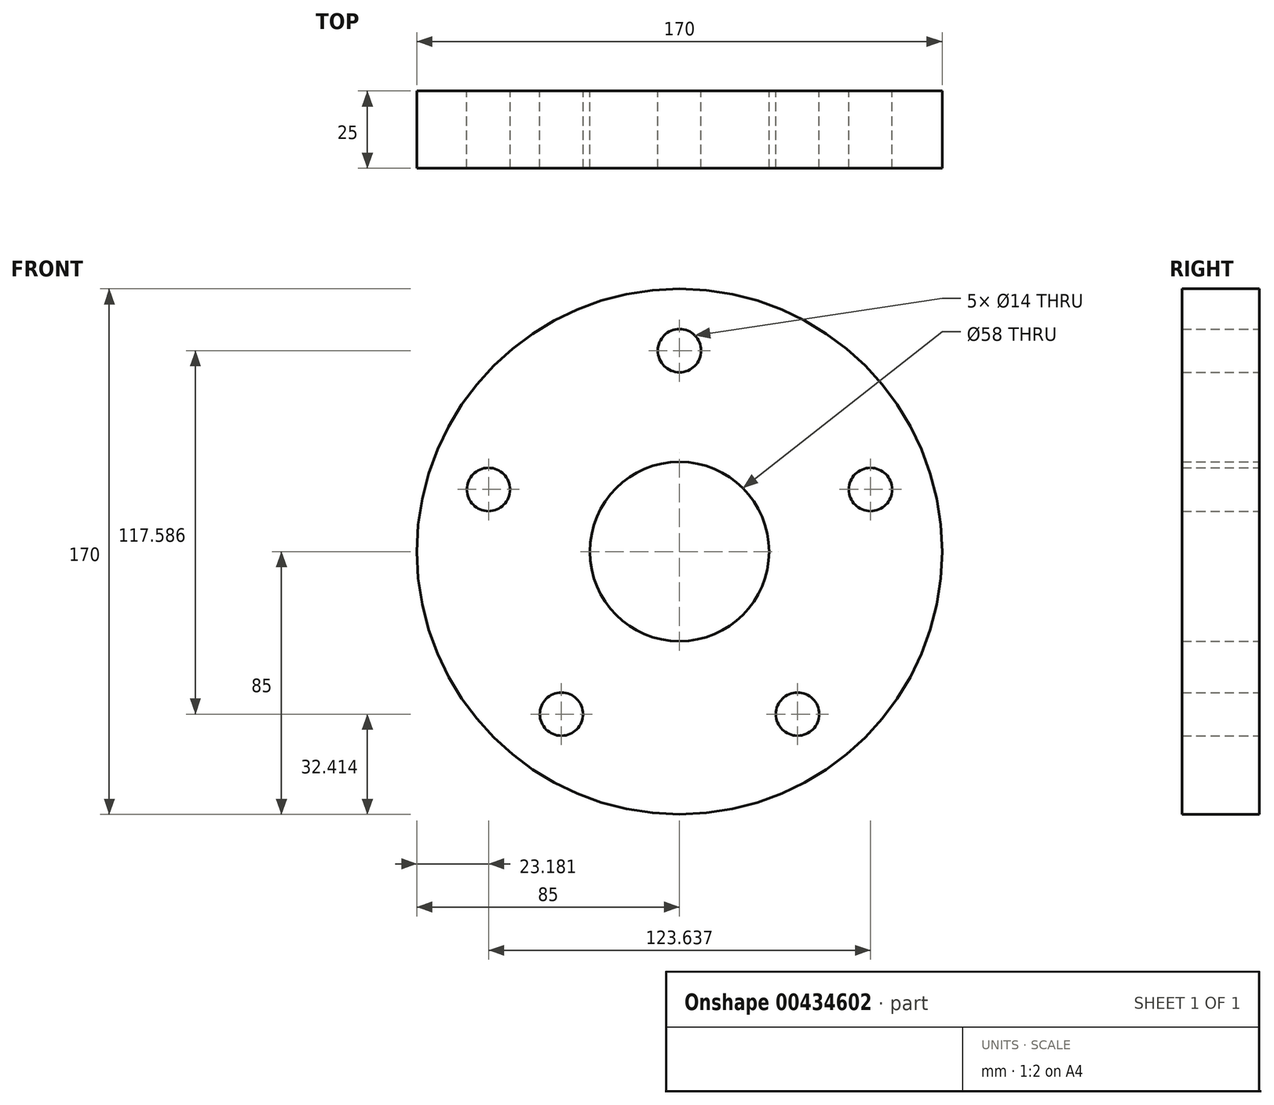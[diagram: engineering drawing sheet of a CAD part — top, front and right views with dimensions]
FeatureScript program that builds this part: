
annotation { "Feature Type Name" : "Feature", "Feature Type Description" : "" }
export const myFeature = defineFeature(function(context is Context, id is Id, definition is map)
    precondition{}
    {
        {
            var Q0;
            Q0=qCreatedBy(makeId("Front.planeOp"),FACE);
            var sketch = newSketch(context, id + "F0", { "sketchPlane" : qUnion([Q0])});
            skCircle(sketch, "E0", {"center": v(0, 0) * mm, "radius": 29 * mm});
            skCircle(sketch, "E1", {"center": v(0, 0) * mm, "radius": 85 * mm});
            skLineSegment(sketch, "E2", {"start": v(0, -97.05) * mm, "end": v(0, 101.44) * mm, "construction": true});
            skCircle(sketch, "E3", {"center": v(0, 65) * mm, "radius": 7 * mm});
            skCircle(sketch, "E4", {"center": v(0, 0) * mm, "radius": 65 * mm, "construction": true});
            skCircle(sketch, "E5.1.0", {"center": v(-61.82, 20.09) * mm, "radius": 7 * mm});
            skCircle(sketch, "E5.2.0", {"center": v(-38.2, -52.59) * mm, "radius": 7 * mm});
            skCircle(sketch, "E5.3.0", {"center": v(38.2, -52.59) * mm, "radius": 7 * mm});
            skCircle(sketch, "E5.4.0", {"center": v(61.82, 20.09) * mm, "radius": 7 * mm});
            skSolve(sketch);
        }
        {
            var Q0;
            Q0 = qSketchRegion(id + "F0", true);
            extrude(context, id + "F1", {"entities" : qUnion([Q0]), "depth" : 25 * mm});
        }
        {
            var Q0;
            Q0=makeQuery(id+"F1.opExtrude","CAP_FACE",FACE,{"disambiguationData":[OSD([sQuery(id+"F0.wireOp",EDGE,"E0"),sQuery(id+"F0.wireOp",EDGE,"E1"),sQuery(id+"F0.wireOp",EDGE,"E3"),sQuery(id+"F0.wireOp",EDGE,"E5.1.0"),sQuery(id+"F0.wireOp",EDGE,"E5.2.0"),sQuery(id+"F0.wireOp",EDGE,"E5.3.0"),sQuery(id+"F0.wireOp",EDGE,"E5.4.0")])],"isStart":false});
            var sketch = newSketch(context, id + "F2", { "sketchPlane" : qUnion([Q0])});
            skLineSegment(sketch, "E6", {"start": v(-92.7, 0) * mm, "end": v(84.19, 0) * mm});
            skCircle(sketch, "E7", {"center": v(-65, 0) * mm, "radius": 7 * mm});
            skCircle(sketch, "E8", {"center": v(0, 0) * mm, "radius": 65 * mm, "construction": true});
            skCircle(sketch, "E9.1.0", {"center": v(0, -65) * mm, "radius": 7 * mm});
            skCircle(sketch, "E9.2.0", {"center": v(65, 0) * mm, "radius": 7 * mm});
            skCircle(sketch, "E9.3.0", {"center": v(0, 65) * mm, "radius": 7 * mm});
            skSolve(sketch);
        }
        {
            var Q0;
            Q0=sQuery(id+"F2.wireOp",EDGE,"E7");
            var Q1;
            Q1=sQuery(id+"F2.wireOp",EDGE,"E9.1.0");
            var Q2;
            Q2=sQuery(id+"F2.wireOp",EDGE,"E9.2.0");
            extrude(context, id + "F3", {"bodyType" : ToolBodyType.SURFACE, "surfaceEntities" : qUnion([Q0, Q1, Q2]), "oppositeDirection" : true, "depth" : 25 * mm});
        }
    });
